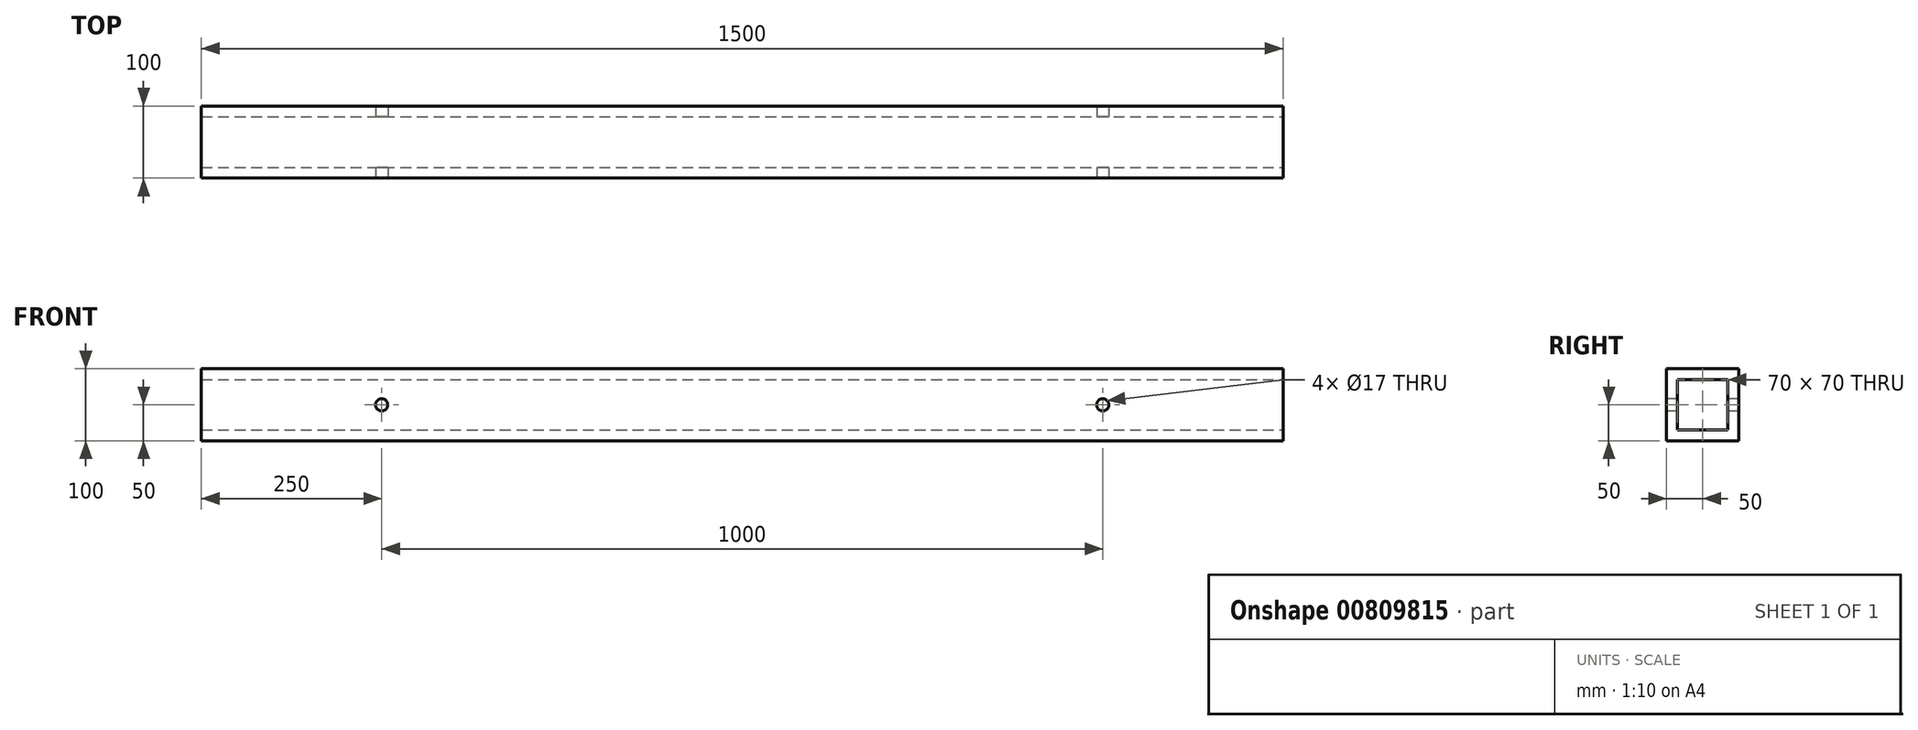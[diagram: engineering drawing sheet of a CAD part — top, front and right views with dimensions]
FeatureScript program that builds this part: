
annotation { "Feature Type Name" : "Feature", "Feature Type Description" : "" }
export const myFeature = defineFeature(function(context is Context, id is Id, definition is map)
    precondition{}
    {
        {
            var Q0;
            Q0=qCreatedBy(makeId("Right.planeOp"),FACE);
            var sketch = newSketch(context, id + "F0", { "sketchPlane" : qUnion([Q0])});
            skLineSegment(sketch, "E0.bottom", {"start": v(-50, 50) * mm, "end": v(50, 50) * mm});
            skLineSegment(sketch, "E0.top", {"start": v(-50, -50) * mm, "end": v(50, -50) * mm});
            skLineSegment(sketch, "E0.left", {"start": v(-50, 50) * mm, "end": v(-50, -50) * mm});
            skLineSegment(sketch, "E0.right", {"start": v(50, 50) * mm, "end": v(50, -50) * mm});
            skSolve(sketch);
        }
        {
            var Q0;
            Q0=makeQuery(id+"F0.imprint","IMPRINT",FACE,{"disambiguationData":[TD([[makeQuery(id+"F0.imprint","IMPRINT",EDGE,{"derivedFrom":sQuery(id+"F0.wireOp",EDGE,"E0.bottom")}),-1.0]])]});
            extrude(context, id + "F1", {"entities" : qUnion([Q0]), "depth" : 1500 * mm, "offsetDistance" : 25 * mm});
        }
        {
            var Q0;
            Q0=makeQuery(id+"F1.opExtrude","CAP_FACE",FACE,{"disambiguationData":[OSD([sQuery(id+"F0.wireOp",EDGE,"E0.bottom"),sQuery(id+"F0.wireOp",EDGE,"E0.top"),sQuery(id+"F0.wireOp",EDGE,"E0.left"),sQuery(id+"F0.wireOp",EDGE,"E0.right")])],"isStart":false});
            var sketch = newSketch(context, id + "F2", { "sketchPlane" : qUnion([Q0])});
            skLineSegment(sketch, "E1.bottom", {"start": v(-35, 35) * mm, "end": v(35, 35) * mm});
            skLineSegment(sketch, "E1.top", {"start": v(-35, -35) * mm, "end": v(35, -35) * mm});
            skLineSegment(sketch, "E1.left", {"start": v(-35, 35) * mm, "end": v(-35, -35) * mm});
            skLineSegment(sketch, "E1.right", {"start": v(35, 35) * mm, "end": v(35, -35) * mm});
            skSolve(sketch);
        }
        {
            var Q0;
            Q0=makeQuery(id+"F2.imprint","IMPRINT",FACE,{"disambiguationData":[TD([[makeQuery(id+"F2.imprint","IMPRINT",EDGE,{"derivedFrom":sQuery(id+"F2.wireOp",EDGE,"E1.bottom")}),-1.0]])]});
            extrude(context, id + "F3", {"entities" : qUnion([Q0]), "operationType" : NewBodyOperationType.REMOVE, "oppositeDirection" : true, "depth" : 2001 * mm, "offsetDistance" : 25 * mm});
        }
        {
            var Q0;
            Q0=makeQuery(id+"F1.opExtrude","SWEPT_FACE",FACE,{"disambiguationData":[OSD([sQuery(id+"F0.wireOp",EDGE,"E0.left")])]});
            var sketch = newSketch(context, id + "F4", { "sketchPlane" : qUnion([Q0])});
            skPoint(sketch, "E2", {"position": v(250, 0) * mm});
            skPoint(sketch, "E3", {"position": v(1250, 0) * mm});
            skSolve(sketch);
        }
        {
            var Q0;
            Q0=sQuery(id+"F4.wireOp",VERTEX,"E2");
            var Q1;
            Q1=sQuery(id+"F4.wireOp",VERTEX,"E3");
            var Q2;
            Q2=makeQuery(id+"F1.opExtrude","SWEPT_BODY",BODY,{"disambiguationData":[OSD([sQuery(id+"F0.wireOp",EDGE,"E0.bottom"),sQuery(id+"F0.wireOp",EDGE,"E0.top"),sQuery(id+"F0.wireOp",EDGE,"E0.left"),sQuery(id+"F0.wireOp",EDGE,"E0.right")])]});
            hole(context, id + "F5", {"style" : HoleStyle.SIMPLE, "endStyle" : HoleEndStyle.THROUGH, "holeDiameter" : 17 * mm, "majorDiameter" : 5 * mm, "isTappedThrough" : true, "tappedDepth" : 12 * mm, "tapClearance" : 3, "locations" : qUnion([Q0, Q1]), "scope" : qUnion([Q2])});
        }
    });
